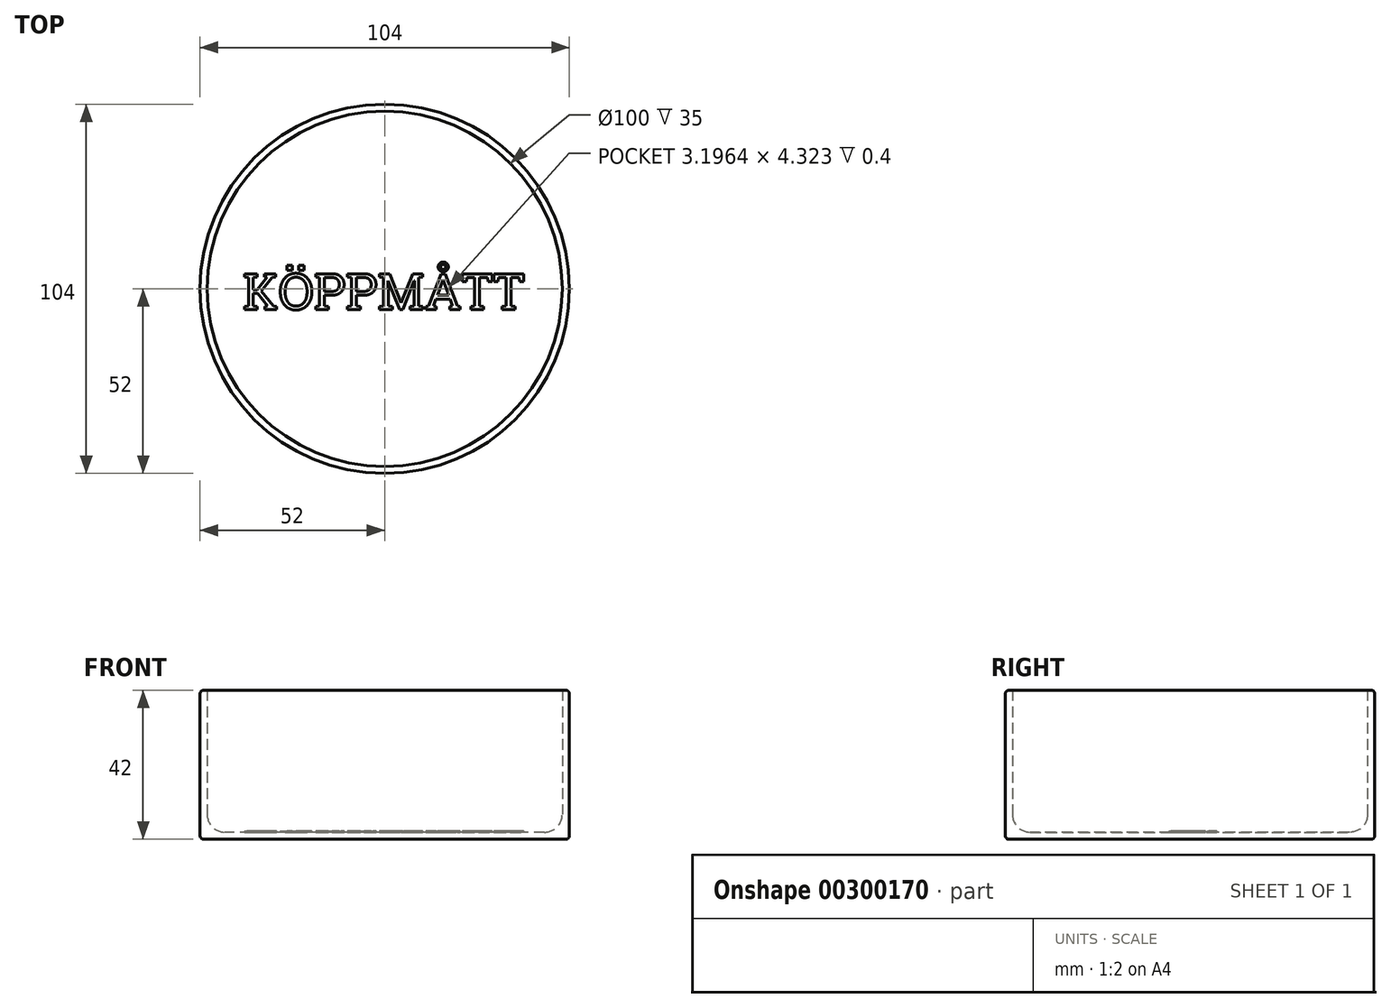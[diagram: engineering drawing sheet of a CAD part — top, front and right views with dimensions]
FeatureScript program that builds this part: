
annotation { "Feature Type Name" : "Feature", "Feature Type Description" : "" }
export const myFeature = defineFeature(function(context is Context, id is Id, definition is map)
    precondition{}
    {
        {
            var Q0;
            Q0=qCreatedBy(makeId("Top.planeOp"),FACE);
            var sketch = newSketch(context, id + "F0", { "sketchPlane" : qUnion([Q0])});
            skCircle(sketch, "E0", {"center": v(0, 0) * mm, "radius": 52 * mm});
            skSolve(sketch);
        }
        {
            var Q0;
            Q0 = qSketchRegion(id + "F0", true);
            extrude(context, id + "F1", {"entities" : qUnion([Q0]), "depth" : 42 * mm});
        }
        {
            var Q0;
            Q0=makeQuery(id+"F1.opExtrude","CAP_FACE",FACE,{"disambiguationData":[OSD([sQuery(id+"F0.wireOp",EDGE,"E0")])],"isStart":false});
            shell(context, id + "F2", {"entities" : qUnion([Q0]), "thickness" : 2 * mm});
        }
        {
            var Q0;
            {var subQ0=sQuery(id+"F0.wireOp",EDGE,"E0");Q0=makeQuery(id+"F2.opShell","OFFSET_EDGE",EDGE,{"disambiguationData":[OSD([subQ0]),TDD([makeQuery(id+"F1.opExtrude","CAP_EDGE",EDGE,{"disambiguationData":[OSD([subQ0])],"isStart":true})])]});}
            fillet(context, id + "F3", {"entities" : qUnion([Q0]), "radius" : 5 * mm, "tangentPropagation" : true, "allowEdgeOverflow" : false});
        }
        {
            var Q0;
            Q0=makeQuery(id+"F1.opExtrude","CAP_EDGE",EDGE,{"disambiguationData":[OSD([sQuery(id+"F0.wireOp",EDGE,"E0")])],"isStart":false});
            fillet(context, id + "F4", {"entities" : qUnion([Q0]), "radius" : 1 * mm, "tangentPropagation" : true, "allowEdgeOverflow" : false});
        }
        {
            var Q0;
            Q0=makeQuery(id+"F1.opExtrude","CAP_EDGE",EDGE,{"disambiguationData":[OSD([sQuery(id+"F0.wireOp",EDGE,"E0")])],"isStart":true});
            fillet(context, id + "F5", {"entities" : qUnion([Q0]), "radius" : 1 * mm, "tangentPropagation" : true, "allowEdgeOverflow" : false});
        }
        {
            var Q0;
            {var subQ0=sQuery(id+"F0.wireOp",EDGE,"E0");Q0=makeQuery(id+"F2.opShell","OFFSET_FACE",FACE,{"disambiguationData":[OSD([subQ0]),TDD([makeQuery(id+"F1.opExtrude","CAP_FACE",FACE,{"disambiguationData":[OSD([subQ0])],"isStart":true})])]});}
            var sketch = newSketch(context, id + "F6", { "sketchPlane" : qUnion([Q0])});
            skText(sketch, "E1", { "text": "KÖPPMÅTT", "fontName": "RobotoSlab-Regular.ttf"});
            const initialGuessF6  = {"E1": [-0.04, -0.00583, 1, 0, 0.0102]};
            skSetInitialGuess(sketch, initialGuessF6);
            skSolve(sketch);
        }
        {
            var Q0;
            Q0 = qSketchRegion(id + "F6", true);
            extrude(context, id + "F7", {"entities" : qUnion([Q0]), "operationType" : NewBodyOperationType.ADD, "depth" : 0.4 * mm});
        }
    });
